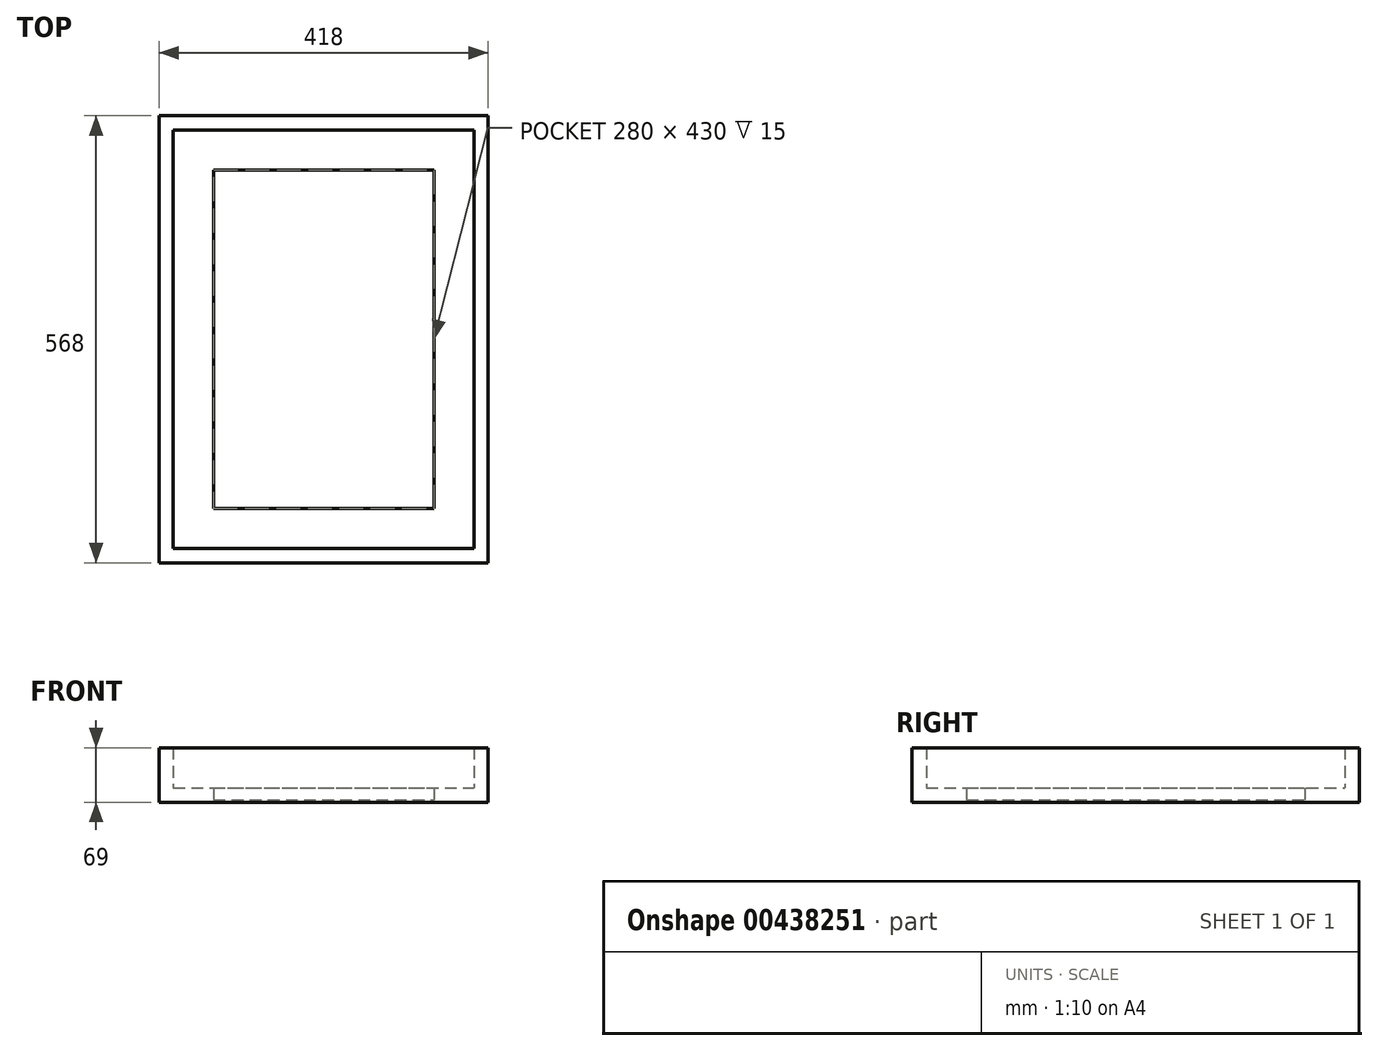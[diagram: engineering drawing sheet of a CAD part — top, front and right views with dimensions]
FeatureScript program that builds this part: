
annotation { "Feature Type Name" : "Feature", "Feature Type Description" : "" }
export const myFeature = defineFeature(function(context is Context, id is Id, definition is map)
    precondition{}
    {
        {
            var Q0;
            Q0=qCreatedBy(makeId("Top.planeOp"),FACE);
            var sketch = newSketch(context, id + "F0", { "sketchPlane" : qUnion([Q0])});
            skLineSegment(sketch, "E0.bottom", {"start": v(-140, -215) * mm, "end": v(140, -215) * mm});
            skLineSegment(sketch, "E0.top", {"start": v(-140, 215) * mm, "end": v(140, 215) * mm});
            skLineSegment(sketch, "E0.left", {"start": v(-140, -215) * mm, "end": v(-140, 215) * mm});
            skLineSegment(sketch, "E0.right", {"start": v(140, -215) * mm, "end": v(140, 215) * mm});
            skPoint(sketch, "E0.middle", {"position": v(0, 0) * mm});
            skLineSegment(sketch, "E1.0", {"start": v(-209, 284) * mm, "end": v(209, 284) * mm});
            skLineSegment(sketch, "E1.1", {"start": v(-209, -284) * mm, "end": v(-209, 284) * mm});
            skLineSegment(sketch, "E1.2", {"start": v(-209, -284) * mm, "end": v(209, -284) * mm});
            skLineSegment(sketch, "E1.3", {"start": v(209, -284) * mm, "end": v(209, 284) * mm});
            skLineSegment(sketch, "E2.0", {"start": v(-191, 266) * mm, "end": v(191, 266) * mm});
            skLineSegment(sketch, "E2.1", {"start": v(-191, -266) * mm, "end": v(-191, 266) * mm});
            skLineSegment(sketch, "E2.2", {"start": v(-191, -266) * mm, "end": v(191, -266) * mm});
            skLineSegment(sketch, "E2.3", {"start": v(191, -266) * mm, "end": v(191, 266) * mm});
            skSolve(sketch);
        }
        {
            var Q0;
            Q0=makeQuery(id+"F0.imprint","IMPRINT",FACE,{"disambiguationData":[TD([[makeQuery(id+"F0.imprint","IMPRINT",EDGE,{"derivedFrom":sQuery(id+"F0.wireOp",EDGE,"E1.0")}),-1.0]])]});
            extrude(context, id + "F1", {"entities" : qUnion([Q0]), "depth" : 69 * mm});
        }
        {
            var Q0;
            Q0=makeQuery(id+"F0.imprint","IMPRINT",FACE,{"disambiguationData":[TD([[makeQuery(id+"F0.imprint","IMPRINT",EDGE,{"derivedFrom":sQuery(id+"F0.wireOp",EDGE,"E1.0")}),-1.0]])]});
            var Q1;
            Q1=makeQuery(id+"F0.imprint","IMPRINT",FACE,{"disambiguationData":[TD([[makeQuery(id+"F0.imprint","IMPRINT",EDGE,{"derivedFrom":sQuery(id+"F0.wireOp",EDGE,"E0.bottom")}),-1.0]])]});
            extrude(context, id + "F2", {"entities" : qUnion([Q0, Q1]), "operationType" : NewBodyOperationType.ADD, "depth" : 18 * mm});
        }
        {
            var Q0;
            Q0=makeQuery(id+"F0.imprint","IMPRINT",FACE,{"disambiguationData":[TD([[makeQuery(id+"F0.imprint","IMPRINT",EDGE,{"derivedFrom":sQuery(id+"F0.wireOp",EDGE,"E0.bottom")}),-1.0]])]});
            var Q1;
            Q1=makeQuery(id+"F0.imprint","IMPRINT",FACE,{"disambiguationData":[TD([[makeQuery(id+"F0.imprint","IMPRINT",EDGE,{"derivedFrom":sQuery(id+"F0.wireOp",EDGE,"E0.bottom")}),1.0]])]});
            extrude(context, id + "F3", {"entities" : qUnion([Q0, Q1]), "operationType" : NewBodyOperationType.ADD, "depth" : 3 * mm});
        }
    });
